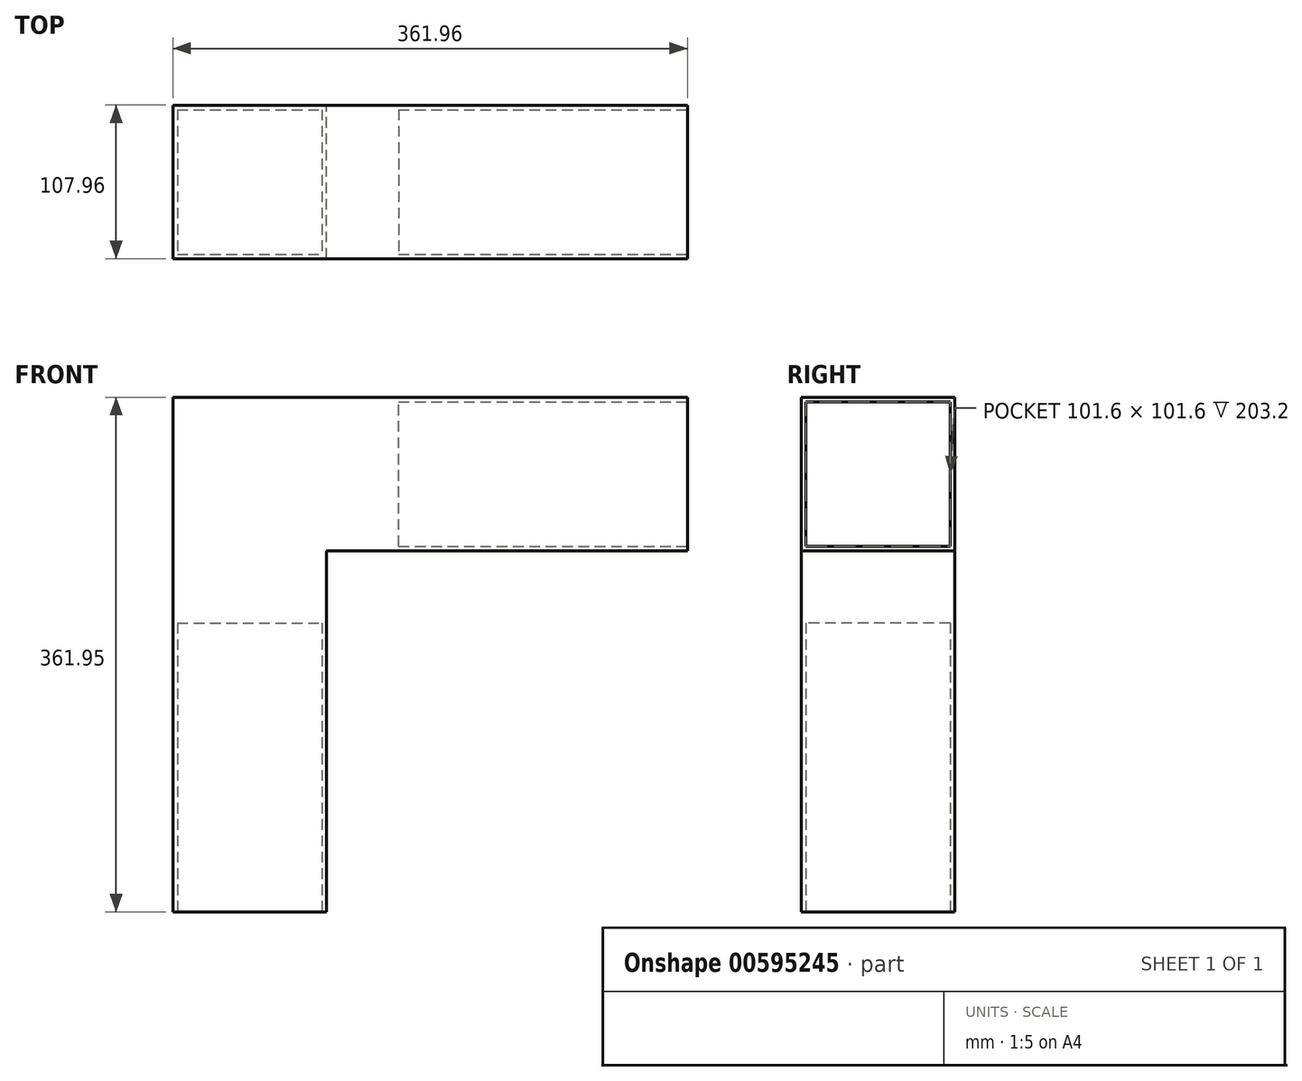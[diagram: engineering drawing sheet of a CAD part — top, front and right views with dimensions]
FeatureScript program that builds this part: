
annotation { "Feature Type Name" : "Feature", "Feature Type Description" : "" }
export const myFeature = defineFeature(function(context is Context, id is Id, definition is map)
    precondition{}
    {
        {
            var Q0;
            Q0=qCreatedBy(makeId("Top.planeOp"),FACE);
            var sketch = newSketch(context, id + "F0", { "sketchPlane" : qUnion([Q0])});
            skLineSegment(sketch, "E0.bottom", {"start": v(53.97, -53.97) * mm, "end": v(-53.98, -53.98) * mm});
            skLineSegment(sketch, "E0.top", {"start": v(53.98, 53.98) * mm, "end": v(-53.97, 53.98) * mm});
            skLineSegment(sketch, "E0.left", {"start": v(53.98, -53.97) * mm, "end": v(53.98, 53.98) * mm});
            skLineSegment(sketch, "E0.right", {"start": v(-53.98, -53.98) * mm, "end": v(-53.97, 53.98) * mm});
            skPoint(sketch, "E0.middle", {"position": v(0, 0) * mm});
            skSolve(sketch);
        }
        {
            var Q0;
            Q0=makeQuery(id+"F0.imprint","IMPRINT",FACE,{"disambiguationData":[TD([[makeQuery(id+"F0.imprint","IMPRINT",EDGE,{"derivedFrom":sQuery(id+"F0.wireOp",EDGE,"E0.bottom")}),-1.0]])]});
            extrude(context, id + "F1", {"entities" : qUnion([Q0]), "depth" : 254 * mm, "offsetDistance" : 25.4 * mm});
        }
        {
            var Q0;
            Q0=makeQuery(id+"F1.opExtrude","SWEPT_FACE",FACE,{"disambiguationData":[OSD([sQuery(id+"F0.wireOp",EDGE,"E0.left")])]});
            var sketch = newSketch(context, id + "F2", { "sketchPlane" : qUnion([Q0])});
            skLineSegment(sketch, "E1.bottom", {"start": v(-53.97, 254) * mm, "end": v(53.98, 254) * mm});
            skLineSegment(sketch, "E1.top", {"start": v(-53.97, 146.05) * mm, "end": v(53.98, 146.05) * mm});
            skLineSegment(sketch, "E1.left", {"start": v(-53.97, 254) * mm, "end": v(-53.97, 146.05) * mm});
            skLineSegment(sketch, "E1.right", {"start": v(53.98, 254) * mm, "end": v(53.98, 146.05) * mm});
            skSolve(sketch);
        }
        {
            var Q0;
            Q0=makeQuery(id+"F2.imprint","IMPRINT",FACE,{"disambiguationData":[TD([[makeQuery(id+"F2.imprint","IMPRINT",EDGE,{"derivedFrom":sQuery(id+"F2.wireOp",EDGE,"E1.bottom")}),-1.0]])]});
            extrude(context, id + "F3", {"entities" : qUnion([Q0]), "operationType" : NewBodyOperationType.ADD, "depth" : 254 * mm, "offsetDistance" : 25.4 * mm});
        }
        {
            var Q0;
            Q0=makeQuery(id+"F1.opExtrude","CAP_FACE",FACE,{"disambiguationData":[OSD([sQuery(id+"F0.wireOp",EDGE,"E0.bottom"),sQuery(id+"F0.wireOp",EDGE,"E0.top"),sQuery(id+"F0.wireOp",EDGE,"E0.left"),sQuery(id+"F0.wireOp",EDGE,"E0.right")])],"isStart":true});
            extrude(context, id + "F4", {"entities" : qUnion([Q0]), "operationType" : NewBodyOperationType.ADD, "depth" : 107.95 * mm, "offsetDistance" : 25.4 * mm});
        }
        {
            var Q0;
            Q0=makeQuery(id+"F4.opExtrude","CAP_FACE",FACE,{"disambiguationData":[OSD([sQuery(id+"F0.wireOp",EDGE,"E0.bottom"),sQuery(id+"F0.wireOp",EDGE,"E0.top"),sQuery(id+"F0.wireOp",EDGE,"E0.left"),sQuery(id+"F0.wireOp",EDGE,"E0.right")])],"isStart":false});
            var sketch = newSketch(context, id + "F5", { "sketchPlane" : qUnion([Q0])});
            skLineSegment(sketch, "E2.bottom", {"start": v(-50.8, -50.8) * mm, "end": v(50.8, -50.8) * mm});
            skLineSegment(sketch, "E2.top", {"start": v(-50.8, 50.8) * mm, "end": v(50.8, 50.8) * mm});
            skLineSegment(sketch, "E2.left", {"start": v(-50.8, -50.8) * mm, "end": v(-50.8, 50.8) * mm});
            skLineSegment(sketch, "E2.right", {"start": v(50.8, -50.8) * mm, "end": v(50.8, 50.8) * mm});
            skPoint(sketch, "E2.middle", {"position": v(0, 0) * mm});
            skSolve(sketch);
        }
        {
            var Q0;
            Q0=makeQuery(id+"F5.imprint","IMPRINT",FACE,{"disambiguationData":[TD([[makeQuery(id+"F5.imprint","IMPRINT",EDGE,{"derivedFrom":sQuery(id+"F5.wireOp",EDGE,"E2.bottom")}),1.0]])]});
            extrude(context, id + "F6", {"entities" : qUnion([Q0]), "operationType" : NewBodyOperationType.REMOVE, "oppositeDirection" : true, "depth" : 203.2 * mm, "offsetDistance" : 25.4 * mm});
        }
        {
            var Q0;
            Q0=makeQuery(id+"F3.opExtrude","CAP_FACE",FACE,{"disambiguationData":[OSD([sQuery(id+"F2.wireOp",EDGE,"E1.bottom"),sQuery(id+"F2.wireOp",EDGE,"E1.top"),sQuery(id+"F2.wireOp",EDGE,"E1.left"),sQuery(id+"F2.wireOp",EDGE,"E1.right")])],"isStart":false});
            var sketch = newSketch(context, id + "F7", { "sketchPlane" : qUnion([Q0])});
            skLineSegment(sketch, "E3.bottom", {"start": v(50.8, 149.22) * mm, "end": v(-50.8, 149.22) * mm});
            skLineSegment(sketch, "E3.top", {"start": v(50.8, 250.83) * mm, "end": v(-50.8, 250.83) * mm});
            skLineSegment(sketch, "E3.left", {"start": v(50.8, 149.22) * mm, "end": v(50.8, 250.83) * mm});
            skLineSegment(sketch, "E3.right", {"start": v(-50.8, 149.22) * mm, "end": v(-50.8, 250.83) * mm});
            skPoint(sketch, "E3.middle", {"position": v(0, 200.03) * mm});
            skPoint(sketch, "E3.middle.positionSnap0", {"position": v(-53.97, 200.03) * mm});
            skPoint(sketch, "E3.centerSnap0", {"position": v(-53.97, 200.03) * mm});
            skSolve(sketch);
        }
        {
            var Q0;
            Q0=makeQuery(id+"F7.imprint","IMPRINT",FACE,{"disambiguationData":[TD([[makeQuery(id+"F7.imprint","IMPRINT",EDGE,{"derivedFrom":sQuery(id+"F7.wireOp",EDGE,"E3.bottom")}),-1.0]])]});
            extrude(context, id + "F8", {"entities" : qUnion([Q0]), "operationType" : NewBodyOperationType.REMOVE, "oppositeDirection" : true, "depth" : 203.2 * mm, "offsetDistance" : 25.4 * mm});
        }
    });
